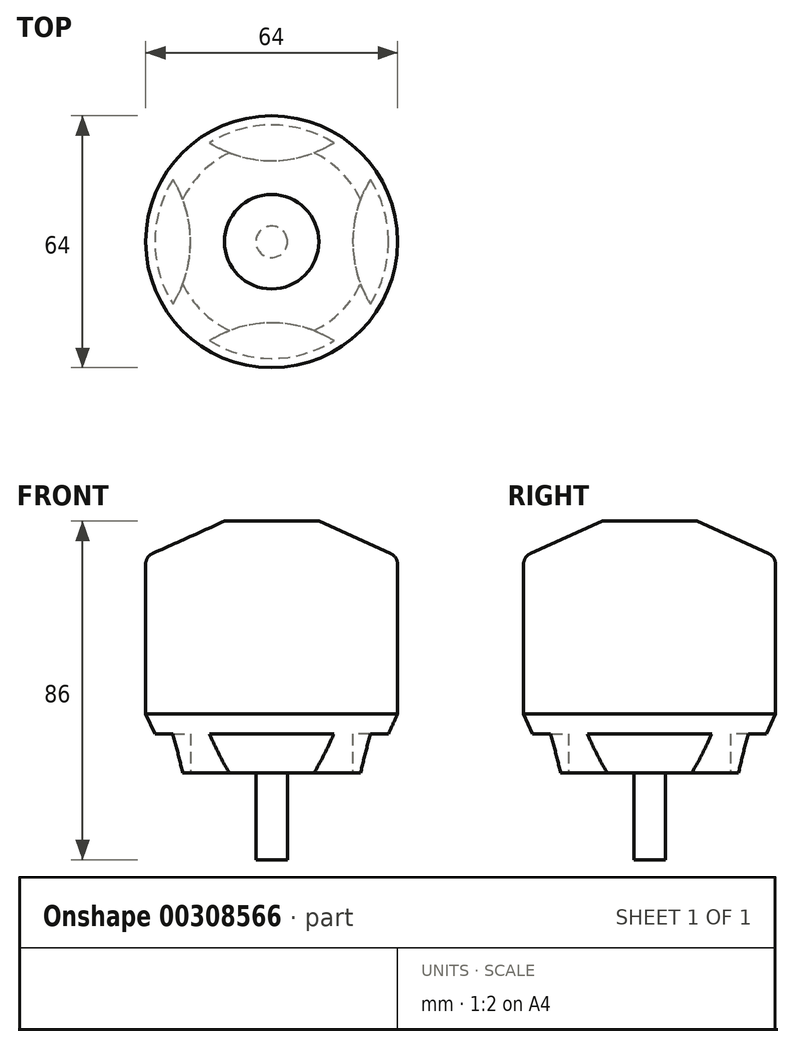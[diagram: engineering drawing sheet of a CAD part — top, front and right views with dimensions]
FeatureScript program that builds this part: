
annotation { "Feature Type Name" : "Feature", "Feature Type Description" : "" }
export const myFeature = defineFeature(function(context is Context, id is Id, definition is map)
    precondition{}
    {
        {
            var Q0;
            Q0=qCreatedBy(makeId("Top.planeOp"),FACE);
            var sketch = newSketch(context, id + "F0", { "sketchPlane" : qUnion([Q0])});
            skCircle(sketch, "E0", {"center": v(0, 0) * mm, "radius": 32 * mm});
            skSolve(sketch);
        }
        {
            var Q0;
            Q0 = qSketchRegion(id + "F0", true);
            extrude(context, id + "F1", {"entities" : qUnion([Q0]), "depth" : 64 * mm});
        }
        {
            var Q0;
            Q0=makeQuery(id+"F1.opExtrude","CAP_EDGE",EDGE,{"disambiguationData":[OSD([sQuery(id+"F0.wireOp",EDGE,"E0")])],"isStart":false});
            chamfer(context, id + "F2", {"entities" : qUnion([Q0]), "chamferType" : ChamferType.TWO_OFFSETS, "width1" : 20 * mm, "oppositeDirection" : false, "width2" : 9 * mm});
        }
        {
            var Q0;
            Q0=makeQuery(id+"F1.opExtrude","CAP_EDGE",EDGE,{"disambiguationData":[OSD([sQuery(id+"F0.wireOp",EDGE,"E0")])],"isStart":true});
            chamfer(context, id + "F3", {"entities" : qUnion([Q0]), "chamferType" : ChamferType.TWO_OFFSETS, "width1" : 15 * mm, "oppositeDirection" : false, "width2" : 7 * mm, "tangentPropagation" : true});
        }
        {
            var Q0;
            {var subQ0=sQuery(id+"F0.wireOp",EDGE,"E0");Q0=makeQuery(id+"F2.opChamfer","BLEND_EDGE",EDGE,{"blendedFrom":[makeQuery(id+"F1.opExtrude","CAP_EDGE",EDGE,{"disambiguationData":[OSD([subQ0])],"isStart":false}),makeQuery(id+"F1.opExtrude","SWEPT_FACE",FACE,{"disambiguationData":[OSD([subQ0])]})],"blendedInto":[makeQuery(id+"F1.opExtrude","SWEPT_FACE",FACE,{"disambiguationData":[OSD([subQ0])]})]});}
            fillet(context, id + "F4", {"entities" : qUnion([Q0]), "radius" : 3 * mm, "tangentPropagation" : true, "allowEdgeOverflow" : false});
        }
        {
            var Q0;
            Q0=makeQuery(id+"F1.opExtrude","CAP_FACE",FACE,{"disambiguationData":[OSD([sQuery(id+"F0.wireOp",EDGE,"E0")])],"isStart":true});
            var sketch = newSketch(context, id + "F5", { "sketchPlane" : qUnion([Q0])});
            skPoint(sketch, "E1", {"position": v(-25, 0) * mm});
            skPoint(sketch, "E2", {"position": v(-50.6, 0) * mm});
            skCircle(sketch, "E3", {"center": v(-50.6, 0) * mm, "radius": 30 * mm});
            skPoint(sketch, "E4.1.0", {"position": v(0, -50.6) * mm});
            skCircle(sketch, "E4.1.1", {"center": v(0, -50.6) * mm, "radius": 30 * mm});
            skPoint(sketch, "E4.2.0", {"position": v(50.6, 0) * mm});
            skCircle(sketch, "E4.2.1", {"center": v(50.6, 0) * mm, "radius": 30 * mm});
            skPoint(sketch, "E4.3.0", {"position": v(0, 50.6) * mm});
            skCircle(sketch, "E4.3.1", {"center": v(0, 50.6) * mm, "radius": 30 * mm});
            skPoint(sketch, "E4.center", {"position": v(0, 0) * mm});
            skSolve(sketch);
        }
        {
            var Q0;
            Q0 = qSketchRegion(id + "F5", true);
            var sketch = newSketch(context, id + "F6", { "sketchPlane" : qUnion([Q0])});
            skCircle(sketch, "E5", {"center": v(0, 0) * mm, "radius": 4 * mm});
            skSolve(sketch);
        }
        {
            var Q0;
            Q0 = qSketchRegion(id + "F5", true);
            extrude(context, id + "F7", {"entities" : qUnion([Q0]), "operationType" : NewBodyOperationType.REMOVE, "oppositeDirection" : true, "depth" : 10 * mm});
        }
        {
            var Q0;
            Q0 = qSketchRegion(id + "F6", true);
            extrude(context, id + "F8", {"entities" : qUnion([Q0]), "operationType" : NewBodyOperationType.ADD, "depth" : 22 * mm});
        }
    });
